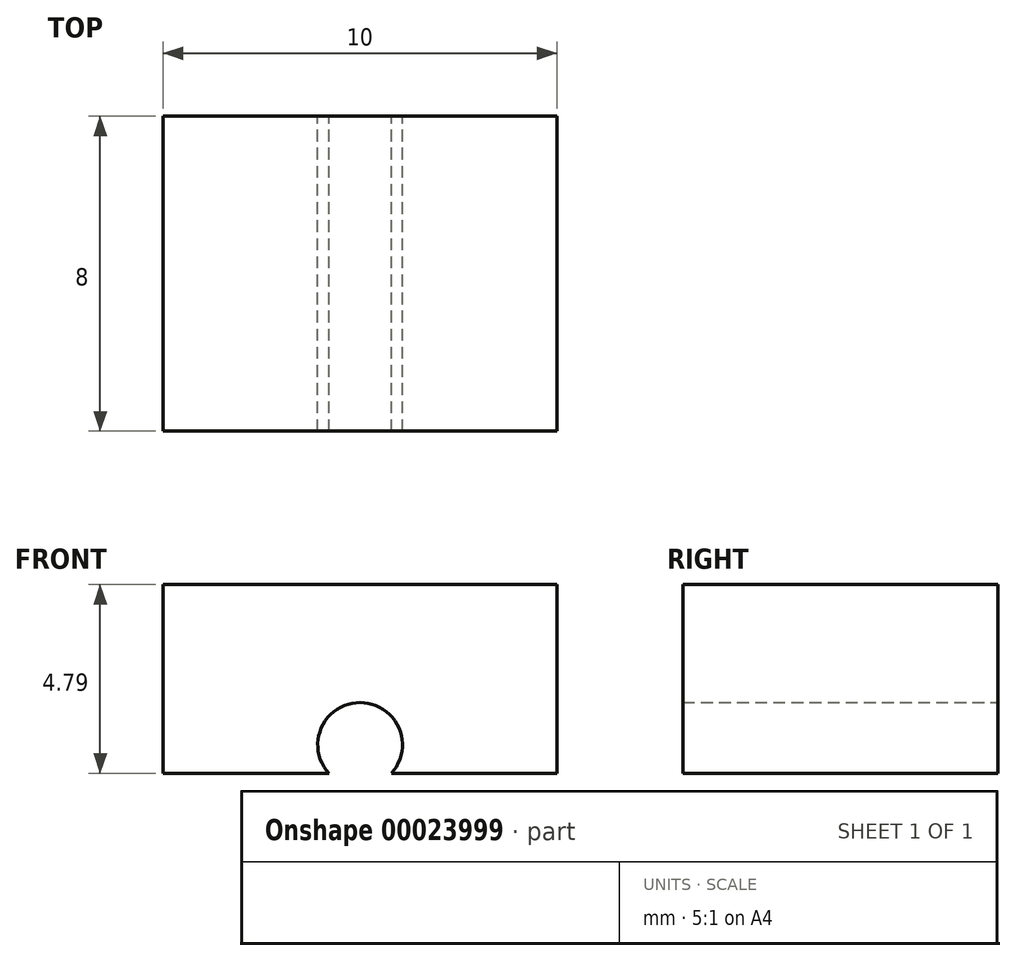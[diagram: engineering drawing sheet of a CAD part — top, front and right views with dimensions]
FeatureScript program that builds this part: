
annotation { "Feature Type Name" : "Feature", "Feature Type Description" : "" }
export const myFeature = defineFeature(function(context is Context, id is Id, definition is map)
    precondition{}
    {
        {
            var Q0;
            Q0=qCreatedBy(makeId("Front.planeOp"),FACE);
            var sketch = newSketch(context, id + "F0", { "sketchPlane" : qUnion([Q0])});
            skArc(sketch, "E0", {"start": v(0.8, -0.72) * mm, "mid": v(0, 1.08) * mm, "end": v(-0.8, -0.72) * mm});
            skLineSegment(sketch, "E1.rect.top", {"start": v(5, 4.08) * mm, "end": v(-5, 4.07) * mm});
            skLineSegment(sketch, "E1.rect.left", {"start": v(5, -0.72) * mm, "end": v(5, 4.08) * mm});
            skLineSegment(sketch, "E1.rect.right", {"start": v(-5, -0.73) * mm, "end": v(-5, 4.07) * mm});
            skLineSegment(sketch, "E2", {"start": v(-0.8, -0.72) * mm, "end": v(-5, -0.73) * mm});
            skLineSegment(sketch, "E3", {"start": v(0.8, -0.72) * mm, "end": v(5, -0.72) * mm});
            skPoint(sketch, "E1.rect.bottom.start.orphan", {"position": v(5, -4.07) * mm});
            skPoint(sketch, "E4.orphan", {"position": v(-5, -4.08) * mm});
            skSolve(sketch);
        }
        {
            var Q0;
            Q0=qSketchRegion(id+"F0",true);
            extrude(context, id + "F1", {"entities" : qUnion([Q0]), "depth" : 8 * mm});
        }
    });
